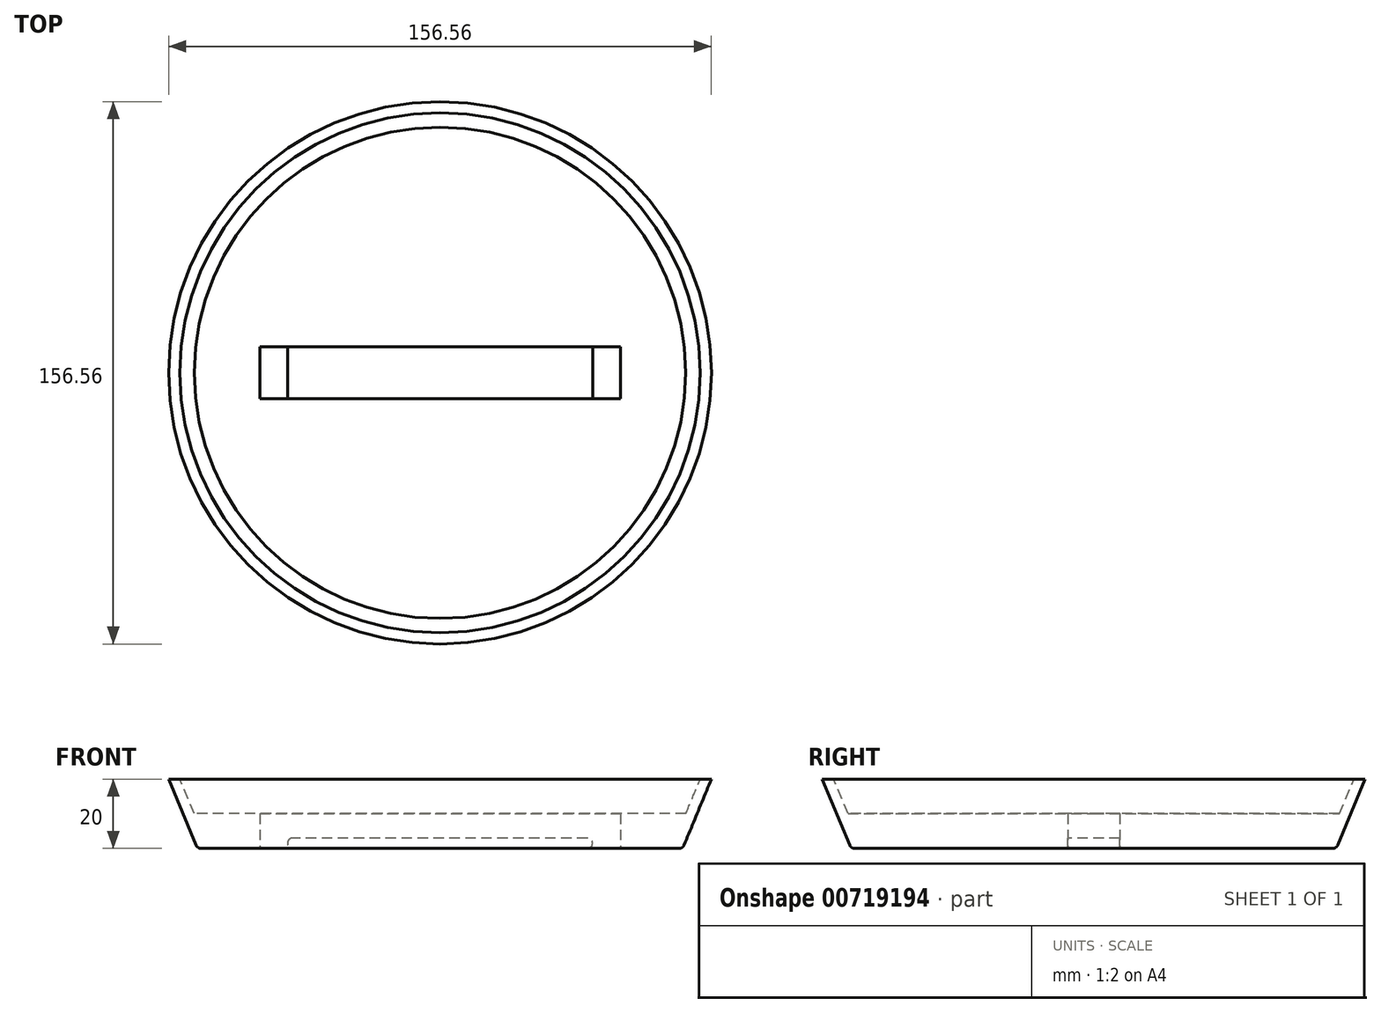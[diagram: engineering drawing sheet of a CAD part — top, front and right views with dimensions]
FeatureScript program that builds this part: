
annotation { "Feature Type Name" : "Feature", "Feature Type Description" : "" }
export const myFeature = defineFeature(function(context is Context, id is Id, definition is map)
    precondition{}
    {
        {
            var Q0;
            Q0=qCreatedBy(makeId("Top.planeOp"),FACE);
            var sketch = newSketch(context, id + "F0", { "sketchPlane" : qUnion([Q0])});
            skLineSegment(sketch, "E0", {"start": v(0, 0) * mm, "end": v(70, 0) * mm, "construction": true});
            skCircle(sketch, "E1", {"center": v(0, 0) * mm, "radius": 70 * mm});
            skLineSegment(sketch, "E2", {"start": v(0, 0) * mm, "end": v(-44, 0) * mm, "construction": true});
            skLineSegment(sketch, "E3", {"start": v(-44, 0) * mm, "end": v(-52, 0) * mm, "construction": true});
            skLineSegment(sketch, "E4", {"start": v(0, 0) * mm, "end": v(0, 7.5) * mm, "construction": true});
            skLineSegment(sketch, "E5", {"start": v(0, 0) * mm, "end": v(0, -7.5) * mm, "construction": true});
            skLineSegment(sketch, "E6", {"start": v(-52, -7.5) * mm, "end": v(-52, 7.5) * mm});
            skLineSegment(sketch, "E7", {"start": v(-52, 7.5) * mm, "end": v(-44, 7.5) * mm});
            skLineSegment(sketch, "E8", {"start": v(-44, 7.5) * mm, "end": v(-44, -7.5) * mm});
            skLineSegment(sketch, "E9", {"start": v(-44, -7.5) * mm, "end": v(-52, -7.5) * mm});
            skLineSegment(sketch, "E10", {"start": v(0, 7.5) * mm, "end": v(44, 7.5) * mm});
            skLineSegment(sketch, "E11", {"start": v(44, 7.5) * mm, "end": v(52, 7.5) * mm});
            skLineSegment(sketch, "E12", {"start": v(52, 7.5) * mm, "end": v(52, -7.5) * mm});
            skLineSegment(sketch, "E13", {"start": v(52, -7.5) * mm, "end": v(44, -7.5) * mm});
            skLineSegment(sketch, "E14", {"start": v(44, 7.5) * mm, "end": v(44, -7.5) * mm});
            skLineSegment(sketch, "E15", {"start": v(0, 7.5) * mm, "end": v(-44, 7.5) * mm});
            skLineSegment(sketch, "E16", {"start": v(44, -7.5) * mm, "end": v(0, -7.5) * mm});
            skLineSegment(sketch, "E17", {"start": v(0, -7.5) * mm, "end": v(-44, -7.5) * mm});
            skSolve(sketch);
        }
        {
            var Q0;
            Q0 = qSketchRegion(id + "F0", true);
            var Q1;
            Q1=makeQuery(id+"F0.imprint","IMPRINT",FACE,{"disambiguationData":[TD([[makeQuery(id+"F0.imprint","IMPRINT",EDGE,{"derivedFrom":sQuery(id+"F0.wireOp",EDGE,"E11")}),-1.0]])]});
            var Q2;
            Q2=makeQuery(id+"F0.imprint","IMPRINT",FACE,{"disambiguationData":[TD([[makeQuery(id+"F0.imprint","IMPRINT",EDGE,{"derivedFrom":sQuery(id+"F0.wireOp",EDGE,"E6")}),-1.0]])]});
            var Q3;
            Q3=makeQuery(id+"F0.imprint","IMPRINT",FACE,{"disambiguationData":[TD([[makeQuery(id+"F0.imprint","IMPRINT",EDGE,{"derivedFrom":sQuery(id+"F0.wireOp",EDGE,"E8")}),1.0]])]});
            extrude(context, id + "F1", {"entities" : qUnion([Q0, Q1, Q2, Q3]), "depth" : 20 * mm, "offsetDistance" : 25 * mm, "hasDraft" : true, "draftAngle" : 22.5 * degree});
        }
        {
            var Q0;
            Q0=makeQuery(id+"F1.opExtrude","CAP_FACE",FACE,{"disambiguationData":[OSD([sQuery(id+"F0.wireOp",EDGE,"E1"),sQuery(id+"F0.wireOp",EDGE,"E6"),sQuery(id+"F0.wireOp",EDGE,"E7"),sQuery(id+"F0.wireOp",EDGE,"E8"),sQuery(id+"F0.wireOp",EDGE,"E9"),sQuery(id+"F0.wireOp",EDGE,"E11"),sQuery(id+"F0.wireOp",EDGE,"E12"),sQuery(id+"F0.wireOp",EDGE,"E13"),sQuery(id+"F0.wireOp",EDGE,"E14")])],"isStart":false});
            shell(context, id + "F2", {"entities" : qUnion([Q0]), "thickness" : 3 * mm});
        }
        {
            var Q0;
            {var subQ0=sQuery(id+"F0.wireOp",EDGE,"E1");Q0=makeQuery(id+"F2.opShell","OFFSET_FACE",FACE,{"disambiguationData":[OSD([subQ0]),TDD([makeQuery(id+"F1.opExtrude","CAP_FACE",FACE,{"disambiguationData":[OSD([subQ0])],"isStart":true})])]});}
            extrude(context, id + "F3", {"entities" : qUnion([Q0]), "operationType" : NewBodyOperationType.ADD, "depth" : 7 * mm, "offsetDistance" : 25 * mm, "hasDraft" : true, "draftAngle" : 22.5 * degree});
        }
        {
            var Q0;
            Q0=makeQuery(id+"F0.imprint","IMPRINT",FACE,{"disambiguationData":[TD([[makeQuery(id+"F0.imprint","IMPRINT",EDGE,{"derivedFrom":sQuery(id+"F0.wireOp",EDGE,"E11")}),-1.0]])]});
            var Q1;
            Q1=makeQuery(id+"F0.imprint","IMPRINT",FACE,{"disambiguationData":[TD([[makeQuery(id+"F0.imprint","IMPRINT",EDGE,{"derivedFrom":sQuery(id+"F0.wireOp",EDGE,"E6")}),-1.0]])]});
            var Q2;
            Q2=makeQuery(id+"F0.imprint","IMPRINT",FACE,{"disambiguationData":[TD([[makeQuery(id+"F0.imprint","IMPRINT",EDGE,{"derivedFrom":sQuery(id+"F0.wireOp",EDGE,"E8")}),1.0]])]});
            extrude(context, id + "F4", {"entities" : qUnion([Q0, Q1, Q2]), "operationType" : NewBodyOperationType.REMOVE, "depth" : 25 * mm, "offsetDistance" : 25 * mm, "hasSecondDirection" : true, "secondDirectionOppositeDirection" : true, "secondDirectionDepth" : 3 * mm});
        }
        {
            var Q0;
            Q0=makeQuery(id+"F0.imprint","IMPRINT",FACE,{"disambiguationData":[TD([[makeQuery(id+"F0.imprint","IMPRINT",EDGE,{"derivedFrom":sQuery(id+"F0.wireOp",EDGE,"E8")}),1.0]])]});
            extrude(context, id + "F5", {"entities" : qUnion([Q0]), "operationType" : NewBodyOperationType.ADD, "depth" : 3 * mm, "offsetDistance" : 25 * mm});
        }
        {
            var Q0;
            Q0=makeQuery(id+"F1.opExtrude","CAP_EDGE",EDGE,{"disambiguationData":[OSD([sQuery(id+"F0.wireOp",EDGE,"E1")])],"isStart":true});
            var Q1;
            Q1=makeQuery(id+"F5.opExtrude","CAP_EDGE",EDGE,{"disambiguationData":[OSD([sQuery(id+"F0.wireOp",EDGE,"E14")])],"isStart":true});
            var Q2;
            Q2=makeQuery(id+"F5.opExtrude","CAP_EDGE",EDGE,{"disambiguationData":[OSD([sQuery(id+"F0.wireOp",EDGE,"E14")])],"isStart":false});
            var Q3;
            Q3=makeQuery(id+"F5.opExtrude","CAP_EDGE",EDGE,{"disambiguationData":[OSD([sQuery(id+"F0.wireOp",EDGE,"E8")])],"isStart":false});
            var Q4;
            Q4=makeQuery(id+"F5.opExtrude","CAP_EDGE",EDGE,{"disambiguationData":[OSD([sQuery(id+"F0.wireOp",EDGE,"E8")])],"isStart":true});
            var Q5;
            Q5=makeQuery(id+"F3.opExtrude","CAP_EDGE",EDGE,{"disambiguationData":[OSD([sQuery(id+"F0.wireOp",EDGE,"E1")])],"isStart":false});
            fillet(context, id + "F6", {"entities" : qUnion([Q0, Q1, Q2, Q3, Q4, Q5]), "radius" : 1.5 * mm, "tangentPropagation" : true, "allowEdgeOverflow" : false});
        }
    });
